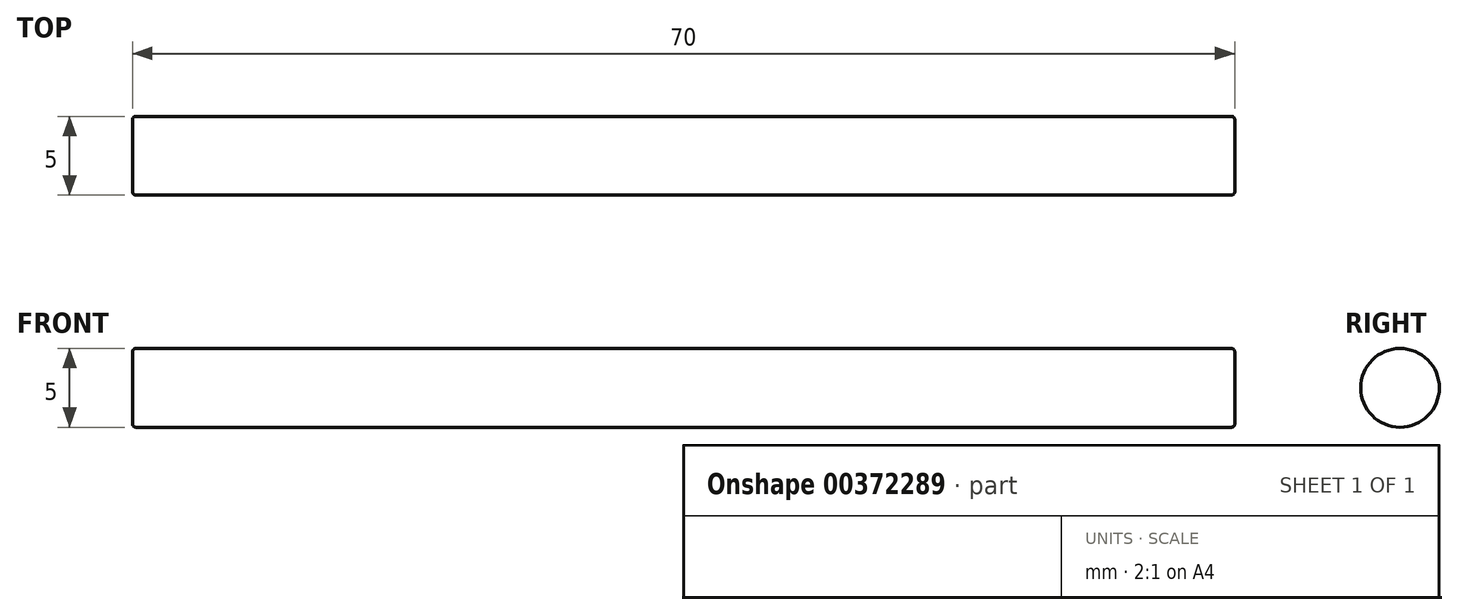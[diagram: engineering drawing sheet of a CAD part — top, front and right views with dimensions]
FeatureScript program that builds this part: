
annotation { "Feature Type Name" : "Feature", "Feature Type Description" : "" }
export const myFeature = defineFeature(function(context is Context, id is Id, definition is map)
    precondition{}
    {
        {
            var Q0;
            Q0=qCreatedBy(makeId("Right.planeOp"),FACE);
            var sketch = newSketch(context, id + "F0", { "sketchPlane" : qUnion([Q0])});
            skCircle(sketch, "E0", {"center": v(0, 0) * mm, "radius": 2.5 * mm});
            skSolve(sketch);
        }
        {
            var Q0;
            Q0=qSketchRegion(id+"F0",true);
            extrude(context, id + "F1", {"entities" : qUnion([Q0]), "depth" : 70 * mm, "symmetric" : true});
        }
        {
            var Q0;
            Q0=makeQuery(id+"F1.opExtrude","CAP_EDGE",EDGE,{"disambiguationData":[OSD([sQuery(id+"F0.wireOp",EDGE,"E0")])],"isStart":false});
            var Q1;
            Q1=makeQuery(id+"F1.opExtrude","CAP_EDGE",EDGE,{"disambiguationData":[OSD([sQuery(id+"F0.wireOp",EDGE,"E0")])],"isStart":true});
            fillet(context, id + "F2", {"entities" : qUnion([Q0, Q1]), "radius" : 0.2 * mm, "tangentPropagation" : true, "allowEdgeOverflow" : false});
        }
    });
